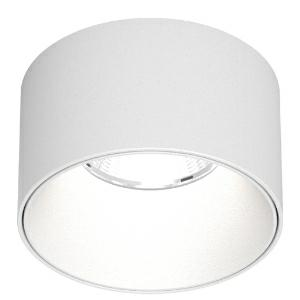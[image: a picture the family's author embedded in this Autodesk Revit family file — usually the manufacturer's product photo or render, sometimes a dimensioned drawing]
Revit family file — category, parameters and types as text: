
# Revit family: invader_semi-on_220-1183
name_source: partatom
category: Lighting Fixtures
units: mm (PartAtom-declared; Revit-internal decimal feet)

## family parameters
Cut with Voids When Loaded = No
Host = Face
Light Source = No
Part Type = Normal
Room Calculation Point = No
Round Connector Dimension = Use Diameter
Shared = No

## types (1)
- 220-1183-H81-W22 (1 x LED, 1182 lm, 13 W, Natural Dim)
    Apparent Load = 13 VA
    CIE Flux Codes = 92 99 100 100 89
    Color Rendering = 1A/90…99
    Color Temperature = Natural Dim
    Default Elevation = 1800 mm
    Description = INVADER SEMI-ON
    Height = 0 mm  [stored 0 ft]
    Lamp = 1 x LED
    Lamp Light Flux = 1182 lm
    Lamp Power = 13 W
    Lamp count = 1
    Length = 75 mm
    Luminous efficacy = 81 lm/W
    Manufacturer = Prolicht
    ModVariant = No
    Model = 220-1183
    Mounting Place = Ceiling
    Mounting Type = Recessed
    Number of Poles = 1
    OnlyDefault = Yes
    Power Factor = 1
    Product Name = INVADER SEMI-ON
    Product group = Recessed spotlights
    ProductGroupID = 422
    Protection Class = Protection class
    Protection Degree = Degree of protection
    RLX_Detail_Level = 1
    RLX_Emergency_Light_Flux = 0 lm
    RLX_Emergency_Type = 0
    RLX_Emergency_Type_DB = No
    RlxData = <blob elided: 125753 chars, md5=4f83fa8b>
    Socket = socket
    Standby Power = 0 W
    System Light Flux = 1052 lm
    System Power = 13 W
    Type Comments = LED COLOUR DIR NATURAL-DIM (81),BEAMWIDTH Spot (22)
    Type Image = 220-1183.jpg
    URL = http://relux.com
    VarID = 220-1183-h81-w22
    Voltage = 0 V
    Weight = 0.00 kg
    Width = 0 mm  [stored 0 ft]

note: [stored X ft] marks values corroborated as IEEE doubles in the binary element streams (Revit-internal decimal feet)

## geometry (parser evidence)
native form markers: Blend x4, Sweep x11
no freeform markers — native parametric forms only
